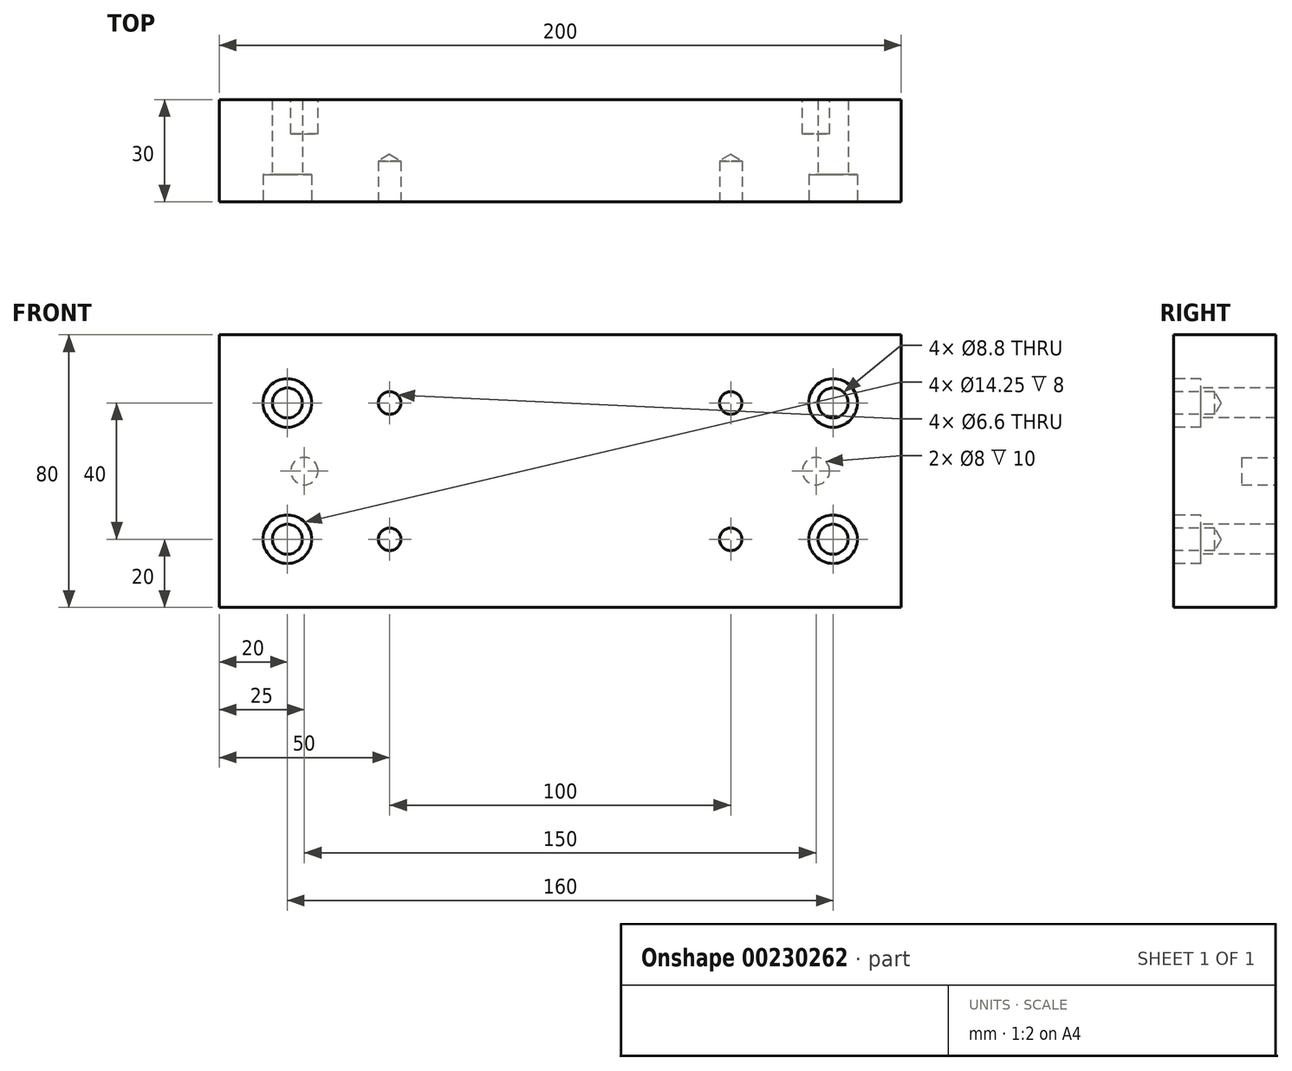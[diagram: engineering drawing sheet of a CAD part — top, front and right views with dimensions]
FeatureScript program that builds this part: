
annotation { "Feature Type Name" : "Feature", "Feature Type Description" : "" }
export const myFeature = defineFeature(function(context is Context, id is Id, definition is map)
    precondition{}
    {
        {
            var Q0;
            Q0=qCreatedBy(makeId("Front.planeOp"),FACE);
            var sketch = newSketch(context, id + "F0", { "sketchPlane" : qUnion([Q0])});
            skLineSegment(sketch, "E0.bottom", {"start": v(100, -40) * mm, "end": v(-100, -40) * mm});
            skLineSegment(sketch, "E0.top", {"start": v(100, 40) * mm, "end": v(-100, 40) * mm});
            skLineSegment(sketch, "E0.left", {"start": v(100, -40) * mm, "end": v(100, 40) * mm});
            skLineSegment(sketch, "E0.right", {"start": v(-100, -40) * mm, "end": v(-100, 40) * mm});
            skPoint(sketch, "E0.middle", {"position": v(0, 0) * mm});
            skSolve(sketch);
        }
        {
            var Q0;
            Q0=makeQuery(id+"F0.imprint","IMPRINT",FACE,{"disambiguationData":[TD([[makeQuery(id+"F0.imprint","IMPRINT",EDGE,{"derivedFrom":sQuery(id+"F0.wireOp",EDGE,"E0.bottom")}),-1.0]])]});
            extrude(context, id + "F1", {"entities" : qUnion([Q0]), "depth" : 30 * mm});
        }
        {
            var Q0;
            Q0=makeQuery(id+"F1.opExtrude","CAP_FACE",FACE,{"disambiguationData":[OSD([sQuery(id+"F0.wireOp",EDGE,"E0.bottom"),sQuery(id+"F0.wireOp",EDGE,"E0.top"),sQuery(id+"F0.wireOp",EDGE,"E0.left"),sQuery(id+"F0.wireOp",EDGE,"E0.right")])],"isStart":true});
            var sketch = newSketch(context, id + "F2", { "sketchPlane" : qUnion([Q0])});
            skCircle(sketch, "E1", {"center": v(-75, 0) * mm, "radius": 4 * mm});
            skCircle(sketch, "E2", {"center": v(75, 0) * mm, "radius": 4 * mm});
            skSolve(sketch);
        }
        {
            var Q0;
            Q0=makeQuery(id+"F2.imprint","IMPRINT",FACE,{"disambiguationData":[TD([[makeQuery(id+"F2.imprint","IMPRINT",EDGE,{"derivedFrom":sQuery(id+"F2.wireOp",EDGE,"E1")}),1.0]])]});
            var Q1;
            Q1=makeQuery(id+"F2.imprint","IMPRINT",FACE,{"disambiguationData":[TD([[makeQuery(id+"F2.imprint","IMPRINT",EDGE,{"derivedFrom":sQuery(id+"F2.wireOp",EDGE,"E2")}),1.0]])]});
            extrude(context, id + "F3", {"entities" : qUnion([Q0, Q1]), "operationType" : NewBodyOperationType.REMOVE, "oppositeDirection" : true, "depth" : 10 * mm});
        }
        {
            var Q0;
            Q0=makeQuery(id+"F1.opExtrude","CAP_FACE",FACE,{"disambiguationData":[OSD([sQuery(id+"F0.wireOp",EDGE,"E0.bottom"),sQuery(id+"F0.wireOp",EDGE,"E0.top"),sQuery(id+"F0.wireOp",EDGE,"E0.left"),sQuery(id+"F0.wireOp",EDGE,"E0.right")])],"isStart":false});
            var sketch = newSketch(context, id + "F4", { "sketchPlane" : qUnion([Q0])});
            skPoint(sketch, "E3", {"position": v(-80, 20) * mm});
            skPoint(sketch, "E4", {"position": v(-80, -20) * mm});
            skPoint(sketch, "E5", {"position": v(80, 20) * mm});
            skPoint(sketch, "E6", {"position": v(80, -20) * mm});
            skSolve(sketch);
        }
        {
            var Q0;
            Q0=sQuery(id+"F4.wireOp",VERTEX,"E3");
            var Q1;
            Q1=sQuery(id+"F4.wireOp",VERTEX,"E4");
            var Q2;
            Q2=sQuery(id+"F4.wireOp",VERTEX,"E5");
            var Q3;
            Q3=sQuery(id+"F4.wireOp",VERTEX,"E6");
            var Q4;
            Q4=makeQuery(id+"F1.opExtrude","SWEPT_BODY",BODY,{"disambiguationData":[OSD([sQuery(id+"F0.wireOp",EDGE,"E0.bottom"),sQuery(id+"F0.wireOp",EDGE,"E0.top"),sQuery(id+"F0.wireOp",EDGE,"E0.left"),sQuery(id+"F0.wireOp",EDGE,"E0.right")])]});
            hole(context, id + "F5", {"style" : HoleStyle.C_BORE, "endStyle" : HoleEndStyle.THROUGH, "standardTappedOrClearance" : lookupTablePath({ "standard" : "ISO", "fit" : "Normal", "size" : "M8", "type" : "Clearance" }), "standardBlindInLast" : lookupTablePath({ "fit" : "Standard", "standard" : "ISO", "size" : "M8", "type" : "Clearance" }), "holeDiameter" : 8.8 * mm, "cBoreDiameter" : 14.25 * mm, "cBoreDepth" : 8 * mm, "locations" : qUnion([Q0, Q1, Q2, Q3]), "scope" : qUnion([Q4]), "isTappedThrough" : true});
        }
        {
            var Q0;
            Q0=makeQuery(id+"F1.opExtrude","CAP_FACE",FACE,{"disambiguationData":[OSD([sQuery(id+"F0.wireOp",EDGE,"E0.bottom"),sQuery(id+"F0.wireOp",EDGE,"E0.top"),sQuery(id+"F0.wireOp",EDGE,"E0.left"),sQuery(id+"F0.wireOp",EDGE,"E0.right")])],"isStart":false});
            var sketch = newSketch(context, id + "F6", { "sketchPlane" : qUnion([Q0])});
            skPoint(sketch, "E7", {"position": v(-50, -20) * mm});
            skPoint(sketch, "E8", {"position": v(-50, 20) * mm});
            skPoint(sketch, "E9", {"position": v(50, 20) * mm});
            skPoint(sketch, "E10", {"position": v(50, -20) * mm});
            skSolve(sketch);
        }
        {
            var Q0;
            Q0=sQuery(id+"F6.wireOp",VERTEX,"E7");
            var Q1;
            Q1=sQuery(id+"F6.wireOp",VERTEX,"E8");
            var Q2;
            Q2=sQuery(id+"F6.wireOp",VERTEX,"E9");
            var Q3;
            Q3=sQuery(id+"F6.wireOp",VERTEX,"E10");
            var Q4;
            Q4=makeQuery(id+"F1.opExtrude","SWEPT_BODY",BODY,{"disambiguationData":[OSD([sQuery(id+"F0.wireOp",EDGE,"E0.bottom"),sQuery(id+"F0.wireOp",EDGE,"E0.top"),sQuery(id+"F0.wireOp",EDGE,"E0.left"),sQuery(id+"F0.wireOp",EDGE,"E0.right")])]});
            hole(context, id + "F7", {"style" : HoleStyle.SIMPLE, "endStyle" : HoleEndStyle.BLIND, "standardTappedOrClearance" : lookupTablePath({ "standard" : "ISO", "fit" : "Normal", "size" : "M6", "type" : "Clearance" }), "standardBlindInLast" : lookupTablePath({ "fit" : "Standard", "standard" : "ISO", "size" : "M6", "type" : "Clearance" }), "holeDiameter" : 6.6 * mm, "holeDepth" : 12 * mm, "locations" : qUnion([Q0, Q1, Q2, Q3]), "scope" : qUnion([Q4])});
        }
    });
